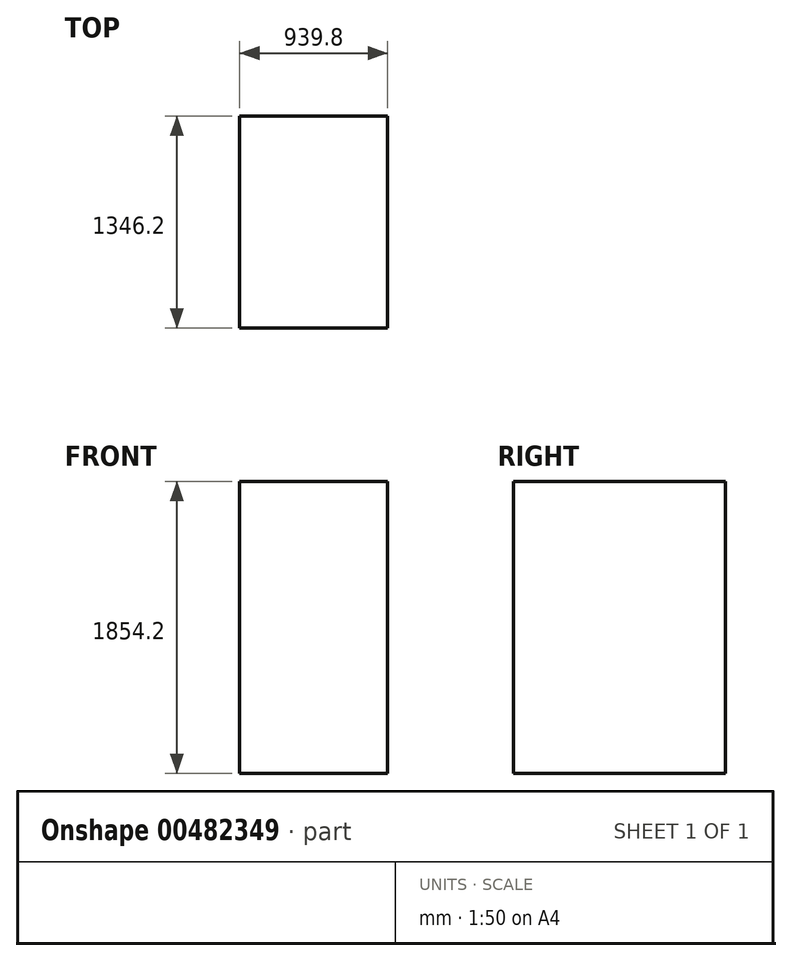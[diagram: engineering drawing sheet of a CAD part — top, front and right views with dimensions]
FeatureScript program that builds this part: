
annotation { "Feature Type Name" : "Feature", "Feature Type Description" : "" }
export const myFeature = defineFeature(function(context is Context, id is Id, definition is map)
    precondition{}
    {
        {
            var Q0;
            Q0=qCreatedBy(makeId("Top.planeOp"),FACE);
            var sketch = newSketch(context, id + "F0", { "sketchPlane" : qUnion([Q0])});
            skLineSegment(sketch, "E0.bottom", {"start": v(0, 0) * mm, "end": v(939.8, 0) * mm});
            skLineSegment(sketch, "E0.top", {"start": v(0, 1346.2) * mm, "end": v(939.8, 1346.2) * mm});
            skLineSegment(sketch, "E0.left", {"start": v(0, 0) * mm, "end": v(0, 1346.2) * mm});
            skLineSegment(sketch, "E0.right", {"start": v(939.8, 0) * mm, "end": v(939.8, 1346.2) * mm});
            skSolve(sketch);
        }
        {
            var Q0;
            Q0 = qSketchRegion(id + "F0", true);
            extrude(context, id + "F1", {"entities" : qUnion([Q0]), "depth" : 1854.2 * mm, "offsetDistance" : 25.4 * mm});
        }
    });
